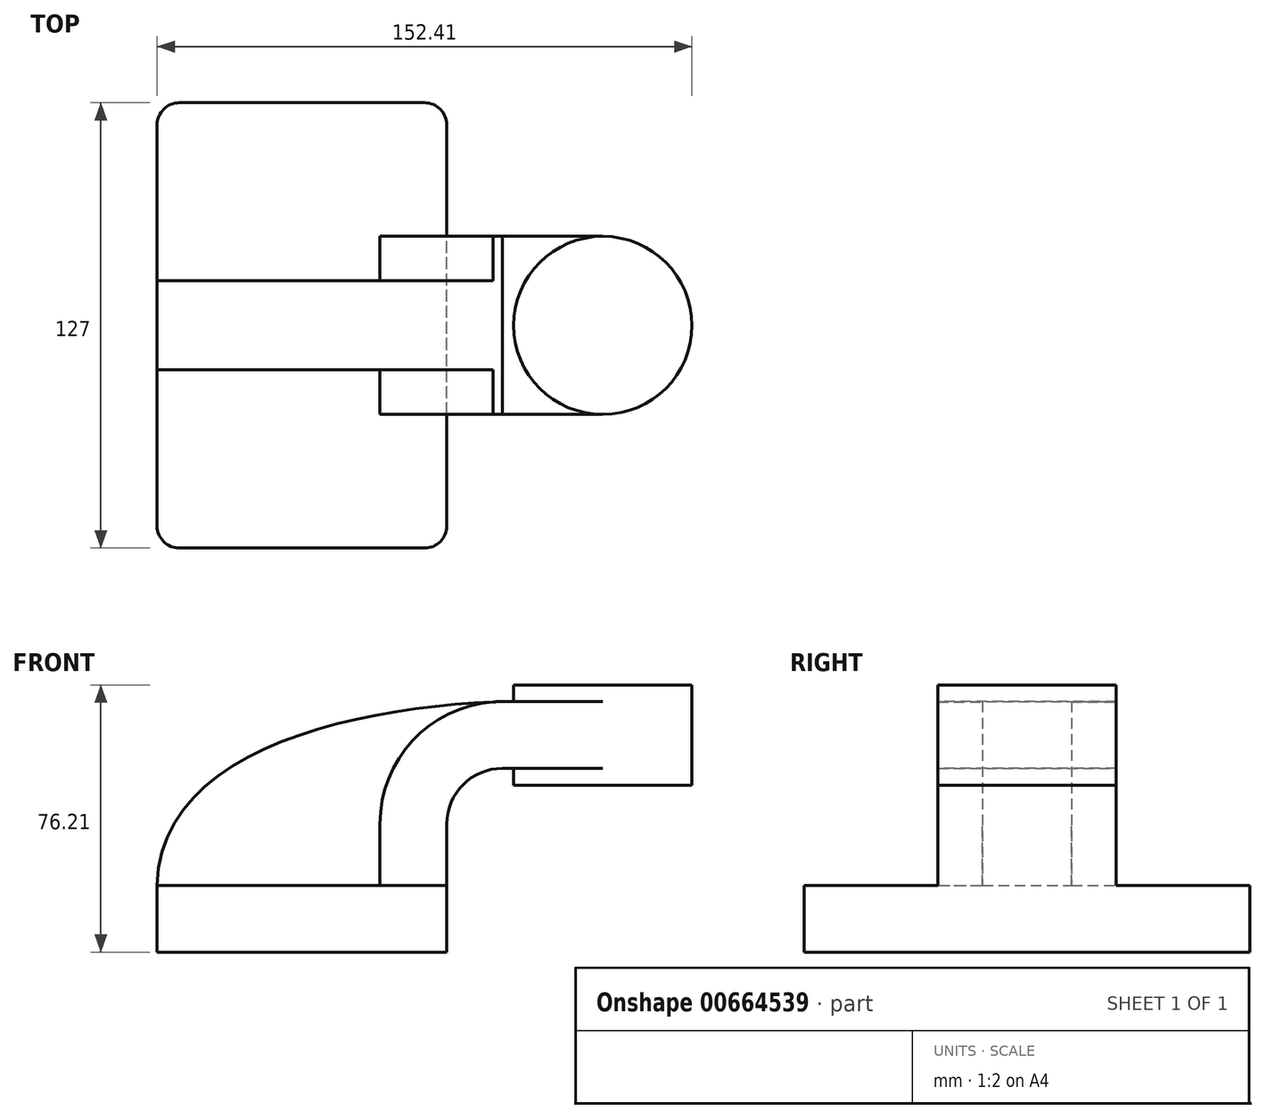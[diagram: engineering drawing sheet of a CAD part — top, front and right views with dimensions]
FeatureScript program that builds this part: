
annotation { "Feature Type Name" : "Feature", "Feature Type Description" : "" }
export const myFeature = defineFeature(function(context is Context, id is Id, definition is map)
    precondition{}
    {
        {
            var Q0;
            Q0=qCreatedBy(makeId("Front.planeOp"),FACE);
            var sketch = newSketch(context, id + "F0", { "sketchPlane" : qUnion([Q0])});
            skLineSegment(sketch, "E0.bottom", {"start": v(41.27, 9.53) * mm, "end": v(-41.27, 9.53) * mm});
            skLineSegment(sketch, "E0.top", {"start": v(41.28, -9.52) * mm, "end": v(-41.27, -9.52) * mm});
            skLineSegment(sketch, "E0.left", {"start": v(41.27, 9.53) * mm, "end": v(41.28, -9.52) * mm});
            skLineSegment(sketch, "E0.right", {"start": v(-41.27, 9.53) * mm, "end": v(-41.27, -9.52) * mm});
            skPoint(sketch, "E0.middle", {"position": v(0, 0) * mm});
            skLineSegment(sketch, "E1.bottom", {"start": v(111.12, 38.1) * mm, "end": v(60.32, 38.1) * mm});
            skLineSegment(sketch, "E1.top", {"start": v(111.12, 66.68) * mm, "end": v(60.32, 66.68) * mm});
            skLineSegment(sketch, "E1.left", {"start": v(111.12, 38.1) * mm, "end": v(111.12, 66.68) * mm});
            skLineSegment(sketch, "E1.right", {"start": v(60.32, 38.1) * mm, "end": v(60.32, 66.68) * mm});
            skPoint(sketch, "E1.middle", {"position": v(85.72, 52.39) * mm});
            skLineSegment(sketch, "E2", {"start": v(41.27, 9.53) * mm, "end": v(41.27, 27) * mm});
            skArc(sketch, "E3", {"start": v(41.27, 27) * mm, "mid": v(45.92, 38.23) * mm, "end": v(57.15, 42.88) * mm});
            skLineSegment(sketch, "E4", {"start": v(57.15, 42.88) * mm, "end": v(85.72, 42.88) * mm});
            skLineSegment(sketch, "E5.0", {"start": v(57.15, 61.93) * mm, "end": v(85.72, 61.93) * mm});
            skArc(sketch, "E5.1", {"start": v(22.22, 27) * mm, "mid": v(32.45, 51.7) * mm, "end": v(57.15, 61.93) * mm});
            skLineSegment(sketch, "E5.2", {"start": v(22.22, 9.53) * mm, "end": v(22.22, 27) * mm});
            skLineSegment(sketch, "E6", {"start": v(85.72, 61.93) * mm, "end": v(85.72, 42.88) * mm});
            skFitSpline(sketch, "E7", {"points": [v(57.15, 61.93) * mm, v(-41.27, 9.52) * mm], "startDerivative": vector(-122.9, -4.06) * mm, "endDerivative": vector(-2.49, -117.71) * mm});
            skLineSegment(sketch, "E8", {"start": v(85.72, 66.68) * mm, "end": v(85.72, 38.1) * mm});
            skSolve(sketch);
        }
        {
            var Q0;
            Q0=makeQuery(id+"F0.imprint","IMPRINT",FACE,{"disambiguationData":[TD([[makeQuery(id+"F0.imprint","IMPRINT",EDGE,{"derivedFrom":sQuery(id+"F0.wireOp",EDGE,"E0.top")}),-1.0]])]});
            extrude(context, id + "F1", {"entities" : qUnion([Q0]), "endBound" : BoundingType.SYMMETRIC, "depth" : (25.4 * 5) * mm, "offsetDistance" : 25 * mm});
        }
        {
            var Q0;
            {var subQ1=sQuery(id+"F0.wireOp",EDGE,"E2");Q0=makeQuery(id+"F0.imprint","IMPRINT",FACE,{"disambiguationData":[TD([[makeQuery(id+"F0.imprint","IMPRINT",EDGE,{"derivedFrom":subQ1}),1.0]])]});}
            var Q1;
            {var subQ5=sQuery(id+"F0.wireOp",EDGE,"E6");Q1=makeQuery(id+"F0.imprint","IMPRINT",FACE,{"disambiguationData":[TD([[makeQuery(id+"F0.imprint","IMPRINT",EDGE,{"derivedFrom":subQ5}),-1.0]])]});}
            var Q2;
            {var subQ0=sQuery(id+"F0.wireOp",EDGE,"E4");var subQ1=sQuery(id+"F0.wireOp",EDGE,"E1.right");var subQ2=makeQuery(id+"F0.imprint","INTERSECT",VERTEX,{"derivedFrom":[subQ1,subQ0]});Q2=makeQuery(id+"F0.imprint","IMPRINT",FACE,{"disambiguationData":[TD([[makeQuery(id+"F0.imprint","IMPRINT",EDGE,{"disambiguationData":[TD([[subQ2,-1.0]])],"derivedFrom":subQ1}),-1.0]])]});}
            extrude(context, id + "F2", {"entities" : qUnion([Q0, Q1, Q2]), "operationType" : NewBodyOperationType.ADD, "endBound" : BoundingType.SYMMETRIC, "depth" : (25.4 * 2) * mm, "offsetDistance" : 25 * mm});
        }
        {
            var Q0;
            {var subQ3=sQuery(id+"F0.wireOp",EDGE,"E5.2");Q0=makeQuery(id+"F0.imprint","IMPRINT",FACE,{"disambiguationData":[TD([[makeQuery(id+"F0.imprint","IMPRINT",EDGE,{"derivedFrom":subQ3}),1.0]])]});}
            extrude(context, id + "F3", {"entities" : qUnion([Q0]), "operationType" : NewBodyOperationType.ADD, "endBound" : BoundingType.SYMMETRIC, "depth" : 25.4 * mm, "offsetDistance" : 25 * mm});
        }
        {
            var Q0;
            {var subQ4=sQuery(id+"F0.wireOp",EDGE,"E1.left");Q0=makeQuery(id+"F0.imprint","IMPRINT",FACE,{"disambiguationData":[TD([[makeQuery(id+"F0.imprint","IMPRINT",EDGE,{"derivedFrom":subQ4}),1.0]])]});}
            var Q1;
            Q1=sQuery(id+"F0.wireOp",EDGE,"E8");
            revolve(context, id + "F4", {"operationType" : NewBodyOperationType.ADD, "entities" : qUnion([Q0]), "axis" : qUnion([Q1]), "revolveType" : RevolveType.FULL});
        }
        {
            var Q0;
            Q0=makeQuery(id+"F1.opExtrude","CAP_EDGE",EDGE,{"disambiguationData":[OSD([sQuery(id+"F0.wireOp",EDGE,"E0.right")])],"isStart":false});
            var Q1;
            Q1=makeQuery(id+"F1.opExtrude","CAP_EDGE",EDGE,{"disambiguationData":[OSD([sQuery(id+"F0.wireOp",EDGE,"E0.left")])],"isStart":false});
            var Q2;
            Q2=makeQuery(id+"F1.opExtrude","CAP_EDGE",EDGE,{"disambiguationData":[OSD([sQuery(id+"F0.wireOp",EDGE,"E0.left")])],"isStart":true});
            var Q3;
            Q3=makeQuery(id+"F1.opExtrude","CAP_EDGE",EDGE,{"disambiguationData":[OSD([sQuery(id+"F0.wireOp",EDGE,"E0.right")])],"isStart":true});
            fillet(context, id + "F5", {"entities" : qUnion([Q0, Q1, Q2, Q3]), "radius" : (25.4 * .25) * mm, "tangentPropagation" : true, "allowEdgeOverflow" : false});
        }
    });
